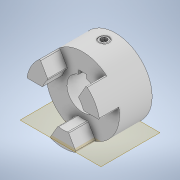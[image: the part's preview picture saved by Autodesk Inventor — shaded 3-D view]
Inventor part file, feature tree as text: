
AUTODESK INVENTOR PART (.ipt)
format: ipt  version: 2021 (Build 250183000, 183)  size: 219,136 bytes
history: native  units: in
note: dims shown in document units (in); Inventor stores cm internally (conversion verified against a paired STEP export)
features: plane x1, extrude x1, sketch x1, other x1, chamfer x1
ambient origin geometry x8: Origin, YZ Plane, XZ Plane, XY Plane, X Axis, Y Axis, Z Axis, Center Point
bodies: Solid1 (feature_tree), Solid2 (feature_tree)
feature tree (5):
  plane  "Work Plane1"
  extrude  "Extrusion1"  Depth=0.375in
  sketch  "Sketch1"  dims[d0=-0.75in d1=0.375in d2=0.5in d3=0.375in d4=0.0in]
  other  "Cut-Extrude2"
  chamfer  "Chamfer4"  Distance=0.5in
